# Revit family: Faucet-Bath-KOHLER-Composed-K-73081
name_source: partatom
category: Plumbing Fixtures
revit_build: Autodesk Revit 2015 (Build: 20140606_1530(x64)
units: mm (PartAtom-declared; Revit-internal decimal feet)

## types (4) — shared parameters
ADA Compliant = Yes
Assembly Code = D2010
CW Connection = Yes
Cold Water Inlet = Cold Water Inlet
Date Modified = 10/05/2018
Default Elevation = 36"
Drain Included = No
Flow Rate = 12 GPM
HW Connection = Yes
Height = 6 1/2"
Hot Water Inlet = Hot Water Inlet
Length = 10 7/16"
Manufacturer = KOHLER Co.
MasterFormat 1995 = 15410
MasterFormat 2004 = 22.41.39
Material = Premium Metal Construction
Pressure = 0.00 psi
Product Documentation Link = http://www.us.kohler.com
Product Name = Composed
Product Page URL = http://www.us.kohler.com
Spout Reach = 8 1/4"
URL = https://www.us.kohler.com
Vent Connection = No
Waste Connection = No
Waste Water Outlet = Waste Water Outlet

## per-type parameters (varying)
| type | 73081_3 | 73081_4 | Description | Finish | Handle Clearance | Model | Type |
| Cross Handle, CP-Polished Chrome | Yes | No | Deck-mount bath faucet with cross handles | Kohler-Metal-CP-Polished_Chrome | 1 17/32" | K-73081-3-CP | 1 |
| Cross Handle, TT-Vibrant Titanium | Yes | No | Deck-mount bath faucet with cross handles | Kohler-Metal-TT-Vibrant_Titanium | 1 17/32" | K-73081-3-TT | 2 |
| Lever Handle, TT-Vibrant Titanium | No | Yes | Deck-mount bath faucet with lever handles | Kohler-Metal-TT-Vibrant_Titanium | 3" | K-73081-4-TT | 4 |
| Lever Handle, CP-Polished Chrome | No | Yes | Deck-mount bath faucet with lever handles | Kohler-Metal-CP-Polished_Chrome | 3" | K-73081-4-CP | 3 |

## geometry (parser evidence)
native form markers: Sweep x10
no freeform markers — native parametric forms only
